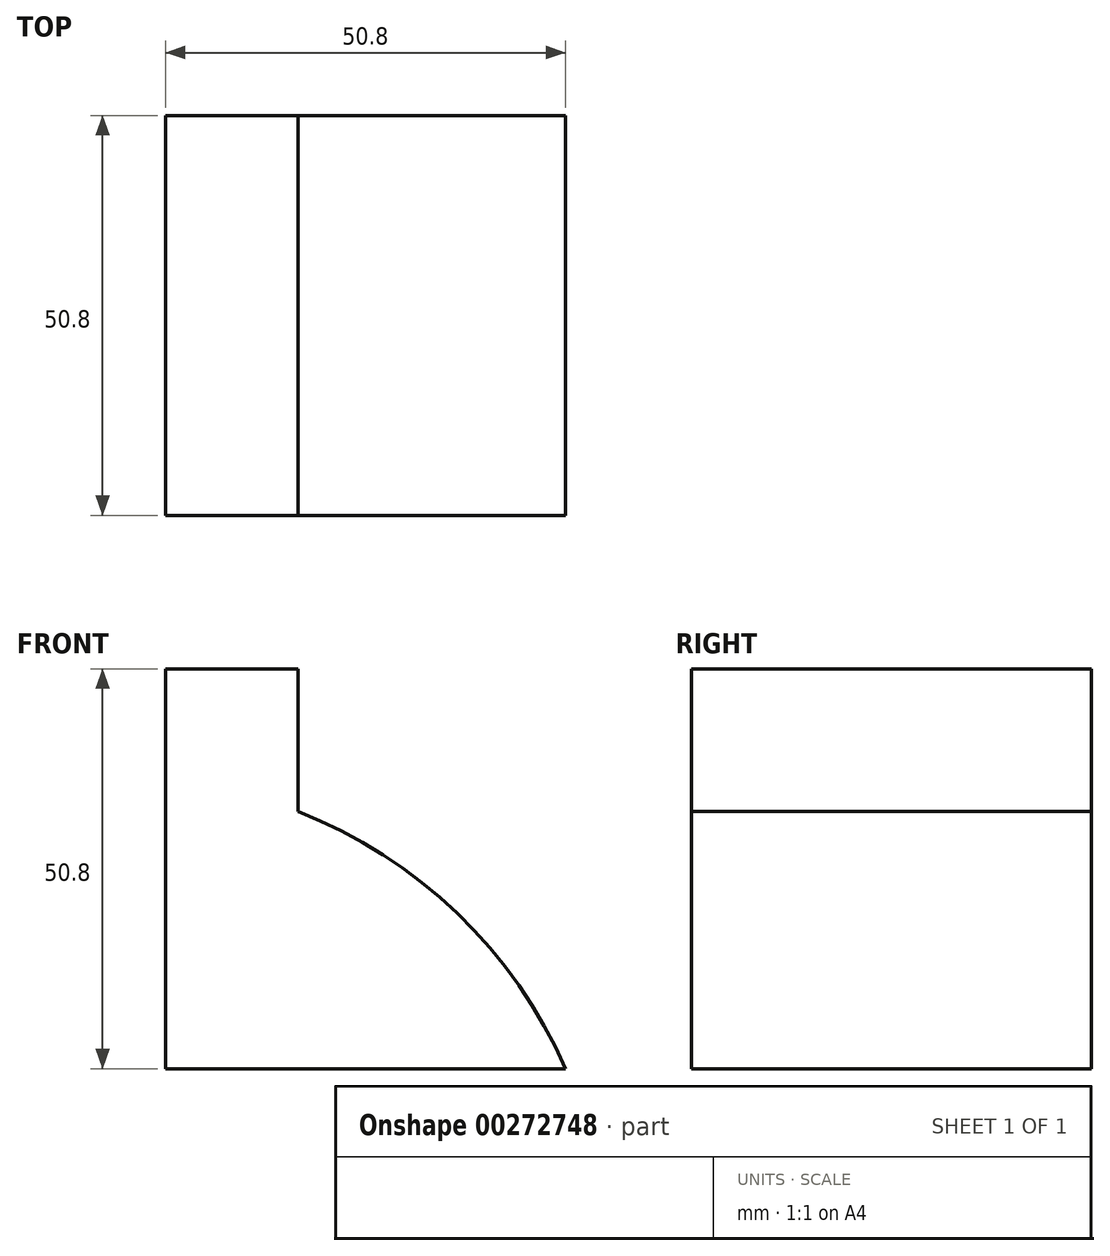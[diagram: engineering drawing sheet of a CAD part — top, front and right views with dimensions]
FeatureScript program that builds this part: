
annotation { "Feature Type Name" : "Feature", "Feature Type Description" : "" }
export const myFeature = defineFeature(function(context is Context, id is Id, definition is map)
    precondition{}
    {
        {
            var Q0;
            Q0=qCreatedBy(makeId("Front.planeOp"),FACE);
            var sketch = newSketch(context, id + "F0", { "sketchPlane" : qUnion([Q0])});
            skLineSegment(sketch, "E0", {"start": v(0, 0) * mm, "end": v(-50.8, 0) * mm});
            skLineSegment(sketch, "E1", {"start": v(-50.8, 0) * mm, "end": v(-50.8, 50.8) * mm});
            skLineSegment(sketch, "E2", {"start": v(-50.8, 50.8) * mm, "end": v(-33.99, 50.8) * mm});
            skLineSegment(sketch, "E3", {"start": v(-33.99, 50.8) * mm, "end": v(-33.99, 32.66) * mm});
            skArc(sketch, "E4", {"start": v(0, 0) * mm, "mid": v(-13.74, 19.72) * mm, "end": v(-33.99, 32.66) * mm});
            skSolve(sketch);
        }
        {
            var Q0;
            Q0=makeQuery(id+"F0.imprint","IMPRINT",FACE,{"disambiguationData":[TD([[makeQuery(id+"F0.imprint","IMPRINT",EDGE,{"derivedFrom":sQuery(id+"F0.wireOp",EDGE,"E0")}),-1.0]])]});
            extrude(context, id + "F1", {"entities" : qUnion([Q0]), "depth" : 50.8 * mm});
        }
    });
